# Revit family: Pantalla Modelo SE_
name_source: partatom
category: Luminarias
units: mm (PartAtom-declared; Revit-internal decimal feet)

## family parameters
Compartido = No
Corte con vacíos al cargar = No
Cota de conector redondo = Diámetro de uso
Origen de luz = No
Punto de cálculo de habitación = No
Se basa en plano de trabajo = Sí
Siempre vertical = No
Tipo de pieza = Normal

## types (4) — shared parameters
Comentarios de vataje = 100-240V
Espesor = 1 mm  [stored 0.00328084 ft]
Fabricante = BRILLANT
zero-valued in all types: Elevación por defecto

## per-type parameters (varying)
| type | Descripción | Lámpara | Modelo | Modulo alto | Modulo largo | Watt per fixture |
| Pantalla Modelo_SE55210W.1 | PANTALLA MODELO SE, CODIGO SE55210W.1, MODELO SE55, PIXEL PITCH 55MM, RESOLUCION DEL PANEL 8X128 DOTS, CANTIDAD POR PANEL DE LED A 1024 DOTS, CONFIGURACION DEL PIXEL SMD 3 EN 1, 1000 NITS EN BRILLO, FRECUENCIA DE ACTUALIZACION A 1000Hz, ESCALA DE GRISES 12BIT, AJUSTE DE BRILLO EN 256 NIVELES, DIMENSION DEL PANEL 440X7040MM, PANEL DE 3.1M2, PESO DEL PANEL EN 9.5kg, MAXIMO CONSUMO DE ENERGIA 350W, PROMEDIO DE CONSUMO 210W, ANGULO DE VISUALIZACION 120/110 GRADOS, DISTANCIA DE VISUALIZACION 55M, TRANSPARENCIA 55%, DURACION DE LAS LUCES (50% BRILLO) >50,000 HORAS, TEMPERATURA DE FUNCIONAMIENTO -30C a +40C, HUMEDAD RELATIVA 10-90%, IP 54/65 (OPCIONAL), VOLTAJE AC 100-240V/50-60Hz, MODO DE ENTRADA CORRIENTE CONSTANTE, TIPO DE SEÑAL AV, S-VIDEO, VGA, CVBS, HDMI, DVI, SDI. REQUIERE ACCESORIOS: PROCESADOR DE VIDEO (XPSE.1), CABLE DE ENERGIA L=75CM (XPSE.2), GANCHO 2.5KG (XPSE.3), DISTRIBUIDOR DE DATOS 8 PUERTOS 15KG (XPSE.5). | SMD 3 en 1 | SE55210W.1 | 7040 mm  [stored 23.0971 ft] | 440 mm  [stored 1.44357 ft] | 350 |
| Pantalla Modelo_SE80160W.1 | PANTALLA MODELO SE, CODIGO SE80160W.1, MODELO SE80, PIXEL PITCH 80MM, RESOLUCION DEL PANEL 8X96 DOTS, CANTIDAD POR PANEL DE LED A 768 DOTS, CONFIGURACION DEL PIXEL SMD 3 EN 1, 600 NITS EN BRILLO, FRECUENCIA DE ACTUALIZACION A 1000Hz, ESCALA DE GRISES 12BIT, AJUSTE DE BRILLO EN 256 NIVELES, DIMENSION DEL PANEL 640X7680MM, PANEL DE 4.9M2, PESO DEL PANEL EN 10.5kg, MAXIMO CONSUMO DE ENERGIA 270W, PROMEDIO DE CONSUMO 160W, ANGULO DE VISUALIZACION 120/110 GRADOS, DISTANCIA DE VISUALIZACION 80M, TRANSPARENCIA 75%, DURACION DE LAS LUCES (50% BRILLO) >50,000 HORAS, TEMPERATURA DE FUNCIONAMIENTO -30C a +40C, HUMEDAD RELATIVA 10-90%, IP 54/65 (OPCIONAL), VOLTAJE AC 100-240V/50-60Hz, MODO DE ENTRADA CORRIENTE CONSTANTE, TIPO DE SEÑAL AV, S-VIDEO, VGA, CVBS, HDMI, DVI, SDI. REQUIERE ACCESORIOS: PROCESADOR DE VIDEO (XPSE.1), CABLE DE ENERGIA L=75CM (XPSE.2), GANCHO 2.5KG (XPSE.3), DISTRIBUIDOR DE DATOS 8 PUERTOS 15KG (XPSE.5). | SMD | SE80160W.1 | 7680 mm  [stored 25.1969 ft] | 640 mm  [stored 2.09974 ft] | 270 |
| Pantalla Modelo_SE55H660W.1 | PANTALLA MODELO SE55H, CODIGO SE55H660W.1, MODELO SE55H, PIXEL PITCH 55MM, RESOLUCION DEL PANEL 8X128 DOTS, CANTIDAD POR PANEL DE LED A 1024 DOTS, CONFIGURACION DEL PIXEL SMD 3 EN 1, 4000 NITS EN BRILLO, FRECUENCIA DE ACTUALIZACION A 1000Hz, ESCALA DE GRISES 12BIT, AJUSTE DE BRILLO EN 256 NIVELES, DIMENSION DEL PANEL 440X7040MM, PANEL DE 3.1M2, PESO DEL PANEL EN 20kg, MAXIMO CONSUMO DE ENERGIA 1100W, PROMEDIO DE CONSUMO 660W, ANGULO DE VISUALIZACION 120/110 GRADOS, DISTANCIA DE VISUALIZACION 55M, TRANSPARENCIA 60%, DURACION DE LAS LUCES (50% BRILLO) >50,000 HORAS, TEMPERATURA DE FUNCIONAMIENTO -30C a +40C, HUMEDAD RELATIVA 10-90%, IP 54/65 (OPCIONAL), VOLTAJE AC 100-240V/50-60Hz, MODO DE ENTRADA CORRIENTE CONSTANTE, TIPO DE SEÑAL AV, S-VIDEO, VGA, CVBS, HDMI, DVI, SDI. REQUIERE ACCESORIOS: PROCESADOR DE VIDEO (XPSE.1), CABLE DE ENERGIA L=75CM (XPSE.2), GANCHO 2.5KG (XPSE.3), DISTRIBUIDOR DE DATOS 8 PUERTOS 15KG (XPSE.5). | SMD | SE55H660W.1 | 7040 mm  [stored 23.0971 ft] | 440 mm  [stored 1.44357 ft] | 1100 |
| Pantalla Modelo_SE80H670W.1 | PANTALLA MODELO SE80H, CODIGO SE80H670W.1, MODELO SE80H, PIXEL PITCH 80MM, RESOLUCION DEL PANEL 8X128 DOTS, CANTIDAD POR PANEL DE LED A 1024 DOTS, CONFIGURACION DEL PIXEL SMD 3 EN 1, 2000 NITS EN BRILLO, FRECUENCIA DE ACTUALIZACION A 1000Hz, ESCALA DE GRISES 12BIT, AJUSTE DE BRILLO EN 256 NIVELES, DIMENSION DEL PANEL 640X10240MM, PANEL DE 6.5M2, PESO DEL PANEL EN 22kg, MAXIMO CONSUMO DE ENERGIA 11,115W, PROMEDIO DE CONSUMO 60W, ANGULO DE VISUALIZACION 120/110 GRADOS, DISTANCIA DE VISUALIZACION 55M, TRANSPARENCIA 60%, DURACION DE LAS LUCES (50% BRILLO) >50,000 HORAS, TEMPERATURA DE FUNCIONAMIENTO -30C a +40C, HUMEDAD RELATIVA 10-90%, IP 54/65 (OPCIONAL), VOLTAJE AC 100-240V/50-60Hz, MODO DE ENTRADA CORRIENTE CONSTANTE, TIPO DE SEÑAL AV, S-VIDEO, VGA, CVBS, HDMI, DVI, SDI. REQUIERE ACCESORIOS: PROCESADOR DE VIDEO (XPSE.1), CABLE DE ENERGIA L=75CM (XPSE.2), GANCHO 2.5KG (XPSE.3), DISTRIBUIDOR DE DATOS 8 PUERTOS 15KG (XPSE.5). | SMD | SE80H670W.1 | 10240 mm  [stored 33.5958 ft] | 640 mm  [stored 2.09974 ft] | 670 |

note: [stored X ft] marks values corroborated as IEEE doubles in the binary element streams (Revit-internal decimal feet)

## geometry (parser evidence)
native form markers: Blend x2
no freeform markers — native parametric forms only
